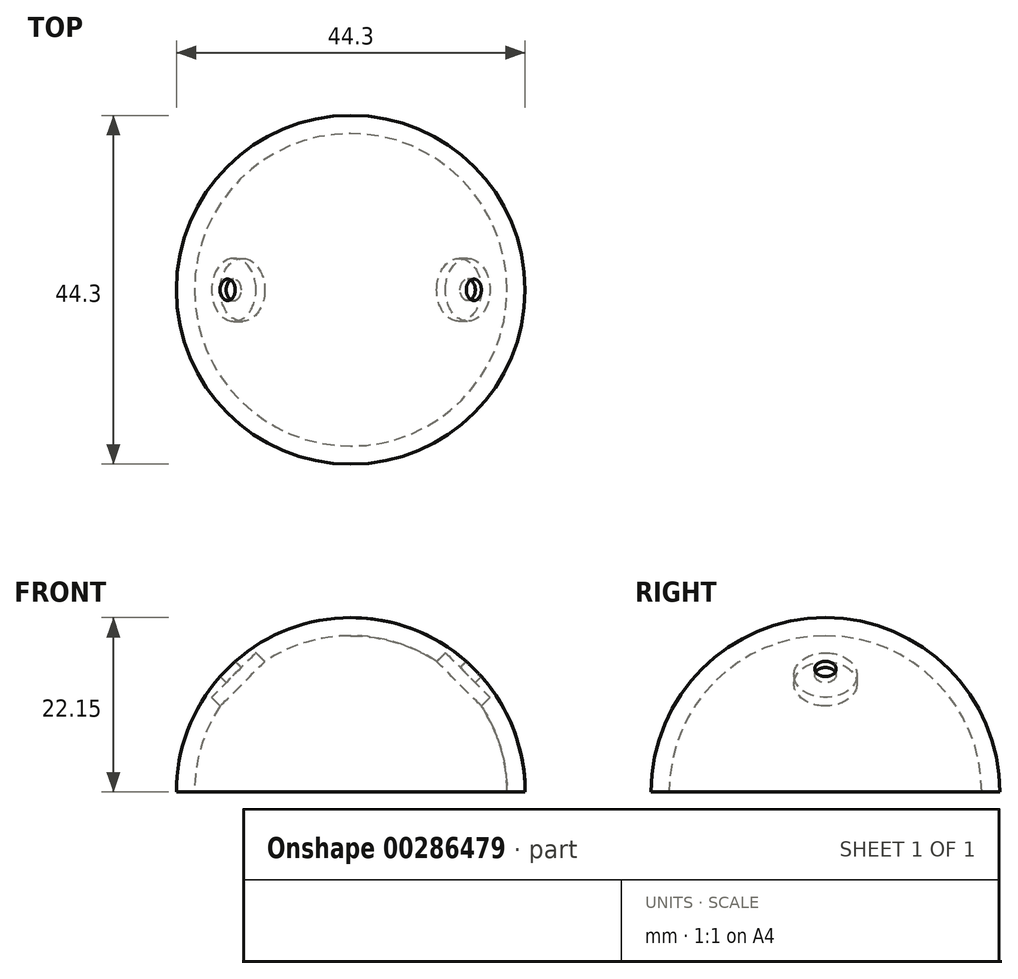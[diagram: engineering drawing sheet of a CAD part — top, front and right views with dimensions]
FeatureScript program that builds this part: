
annotation { "Feature Type Name" : "Feature", "Feature Type Description" : "" }
export const myFeature = defineFeature(function(context is Context, id is Id, definition is map)
    precondition{}
    {
        {
            var Q0;
            Q0=qCreatedBy(makeId("Front.planeOp"),FACE);
            var sketch = newSketch(context, id + "F0", { "sketchPlane" : qUnion([Q0])});
            skArc(sketch, "E0", {"start": v(22.15, 0) * mm, "mid": v(0, 22.15) * mm, "end": v(-22.15, 0) * mm});
            skLineSegment(sketch, "E1", {"start": v(0, 0) * mm, "end": v(-15.66, 15.66) * mm, "construction": true});
            skLineSegment(sketch, "E2.MirrorCS", {"start": v(0, 0) * mm, "end": v(15.66, 15.66) * mm});
            skArc(sketch, "E3.0", {"start": v(19.85, 0) * mm, "mid": v(0, 19.85) * mm, "end": v(-19.85, 0) * mm});
            skLineSegment(sketch, "E4", {"start": v(-22.15, 0) * mm, "end": v(-19.85, 0) * mm});
            skLineSegment(sketch, "E5", {"start": v(0, 19.85) * mm, "end": v(0, 22.15) * mm});
            skPoint(sketch, "E6", {"position": v(-14.04, 14.04) * mm});
            skPoint(sketch, "E7", {"position": v(14.04, 14.04) * mm});
            skLineSegment(sketch, "E8", {"start": v(15.66, 15.66) * mm, "end": v(14.7, 16.63) * mm});
            skLineSegment(sketch, "E9", {"start": v(14.7, 16.63) * mm, "end": v(13.9, 15.82) * mm});
            skLineSegment(sketch, "E10", {"start": v(13.9, 15.82) * mm, "end": v(12.03, 17.69) * mm});
            skLineSegment(sketch, "E11", {"start": v(12.03, 17.69) * mm, "end": v(8.5, 14.15) * mm});
            skLineSegment(sketch, "E12", {"start": v(8.5, 14.15) * mm, "end": v(11.32, 11.32) * mm});
            skSolve(sketch);
        }
        {
            var Q0;
            {var subQ0=sQuery(id+"F0.wireOp",EDGE,"E4");Q0=makeQuery(id+"F0.imprint","IMPRINT",FACE,{"disambiguationData":[TD([[makeQuery(id+"F0.imprint","IMPRINT",EDGE,{"derivedFrom":subQ0}),1.0]])]});}
            var Q1;
            Q1=sQuery(id+"F0.wireOp",EDGE,"E5");
            revolve(context, id + "F1", {"surfaceOperationType" : NewSurfaceOperationType.NEW, "entities" : qUnion([Q0]), "axis" : qUnion([Q1]), "revolveType" : RevolveType.FULL});
        }
        {
            var Q0;
            {var subQ0=sQuery(id+"F0.wireOp",EDGE,"E12");Q0=makeQuery(id+"F0.imprint","IMPRINT",FACE,{"disambiguationData":[TD([[makeQuery(id+"F0.imprint","IMPRINT",EDGE,{"derivedFrom":subQ0}),1.0]])]});}
            var Q1;
            {var subQ3=sQuery(id+"F0.wireOp",EDGE,"E10");Q1=makeQuery(id+"F0.imprint","IMPRINT",FACE,{"disambiguationData":[TD([[makeQuery(id+"F0.imprint","IMPRINT",EDGE,{"derivedFrom":subQ3}),1.0]])]});}
            var Q2;
            Q2=sQuery(id+"F0.wireOp",EDGE,"E2.MirrorCS");
            revolve(context, id + "F2", {"surfaceOperationType" : NewSurfaceOperationType.NEW, "entities" : qUnion([Q0, Q1]), "axis" : qUnion([Q2]), "revolveType" : RevolveType.FULL});
        }
        {
            var Q0;
            Q0=makeQuery(id+"F2.opRevolve","SWEPT_BODY",BODY,{"disambiguationData":[OSD([sQuery(id+"F0.wireOp",EDGE,"E0"),sQuery(id+"F0.wireOp",EDGE,"E2.MirrorCS"),sQuery(id+"F0.wireOp",EDGE,"E9"),sQuery(id+"F0.wireOp",EDGE,"E10"),sQuery(id+"F0.wireOp",EDGE,"E11"),sQuery(id+"F0.wireOp",EDGE,"E12")])]});
            var Q1;
            Q1=qCreatedBy(makeId("Right.planeOp"),FACE);
            mirror(context, id + "F3", {"operationType" : NewBodyOperationType.REMOVE, "entities" : qUnion([Q0]), "mirrorPlane" : qUnion([Q1])});
        }
        {
            var Q0;
            Q0=makeQuery(id+"F2.opRevolve","SWEPT_BODY",BODY,{"disambiguationData":[OSD([sQuery(id+"F0.wireOp",EDGE,"E0"),sQuery(id+"F0.wireOp",EDGE,"E2.MirrorCS"),sQuery(id+"F0.wireOp",EDGE,"E9"),sQuery(id+"F0.wireOp",EDGE,"E10"),sQuery(id+"F0.wireOp",EDGE,"E11"),sQuery(id+"F0.wireOp",EDGE,"E12")])]});
            var Q1;
            Q1=makeQuery(id+"F1.opRevolve","SWEPT_BODY",BODY,{"disambiguationData":[OSD([sQuery(id+"F0.wireOp",EDGE,"E0"),sQuery(id+"F0.wireOp",EDGE,"E3.0"),sQuery(id+"F0.wireOp",EDGE,"E4"),sQuery(id+"F0.wireOp",EDGE,"E5")])]});
            booleanBodies(context, id + "F4", {"operationType" : BooleanOperationType.SUBTRACTION, "tools" : qUnion([Q0]), "targets" : qUnion([Q1])});
        }
    });
